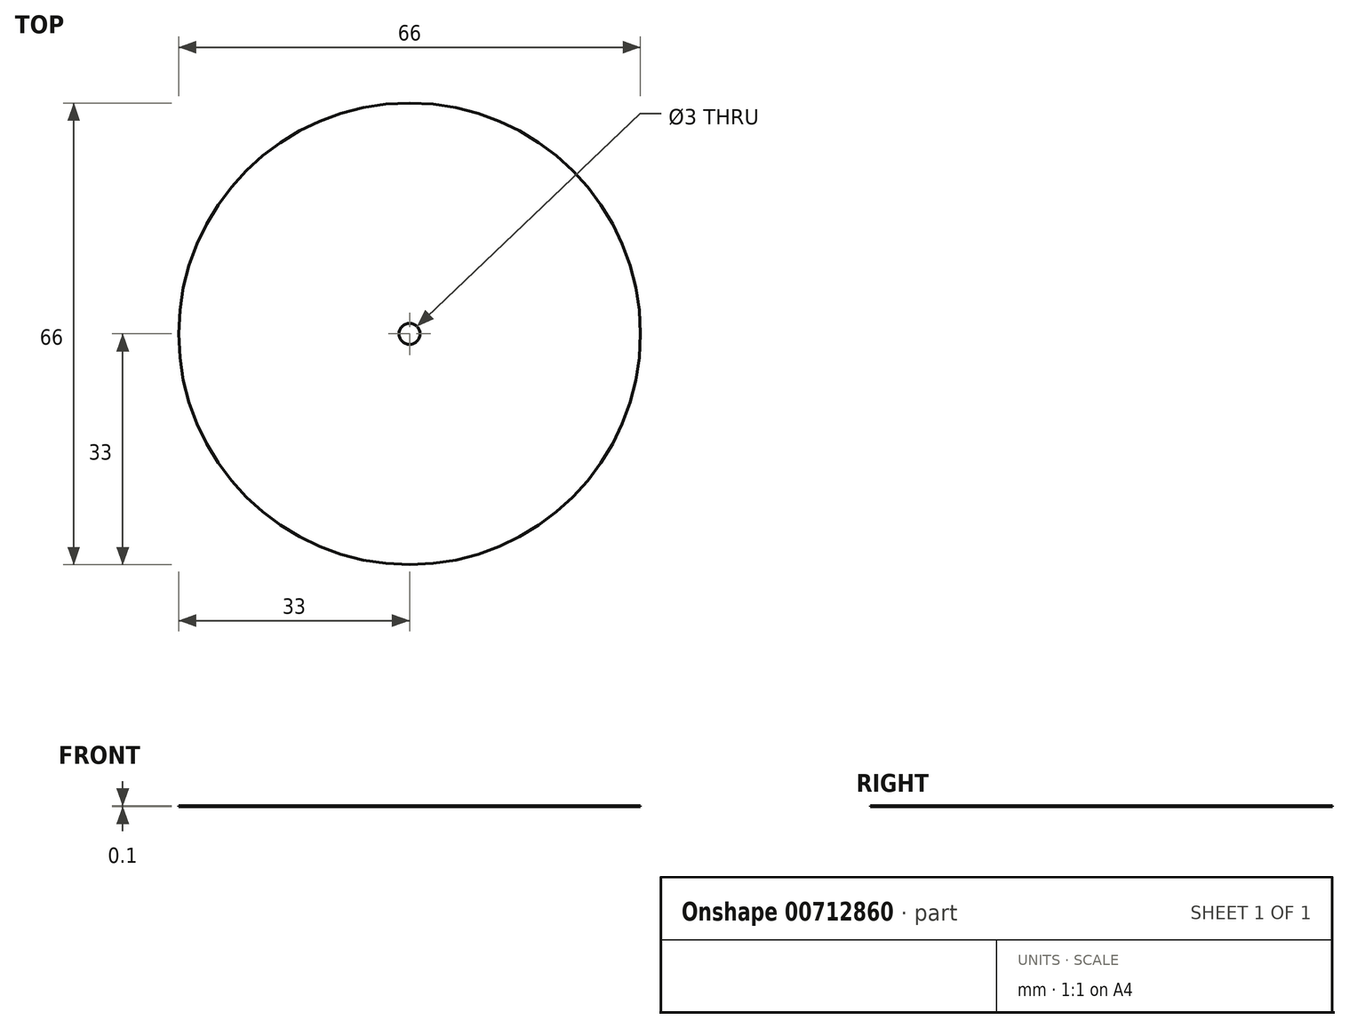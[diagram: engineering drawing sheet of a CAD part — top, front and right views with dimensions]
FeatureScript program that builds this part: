
annotation { "Feature Type Name" : "Feature", "Feature Type Description" : "" }
export const myFeature = defineFeature(function(context is Context, id is Id, definition is map)
    precondition{}
    {
        {
            var Q0;
            Q0=qCreatedBy(makeId("Top.planeOp"),FACE);
            var sketch = newSketch(context, id + "F0", { "sketchPlane" : qUnion([Q0])});
            skCircle(sketch, "E0", {"center": v(0, 0) * mm, "radius": 33 * mm});
            skCircle(sketch, "E1", {"center": v(0, 0) * mm, "radius": 1.5 * mm});
            skSolve(sketch);
        }
        {
            var Q0;
            Q0 = qSketchRegion(id + "F0", true);
            extrude(context, id + "F1", {"entities" : qUnion([Q0]), "depth" : 0.1 * mm, "offsetDistance" : 25 * mm});
        }
    });
